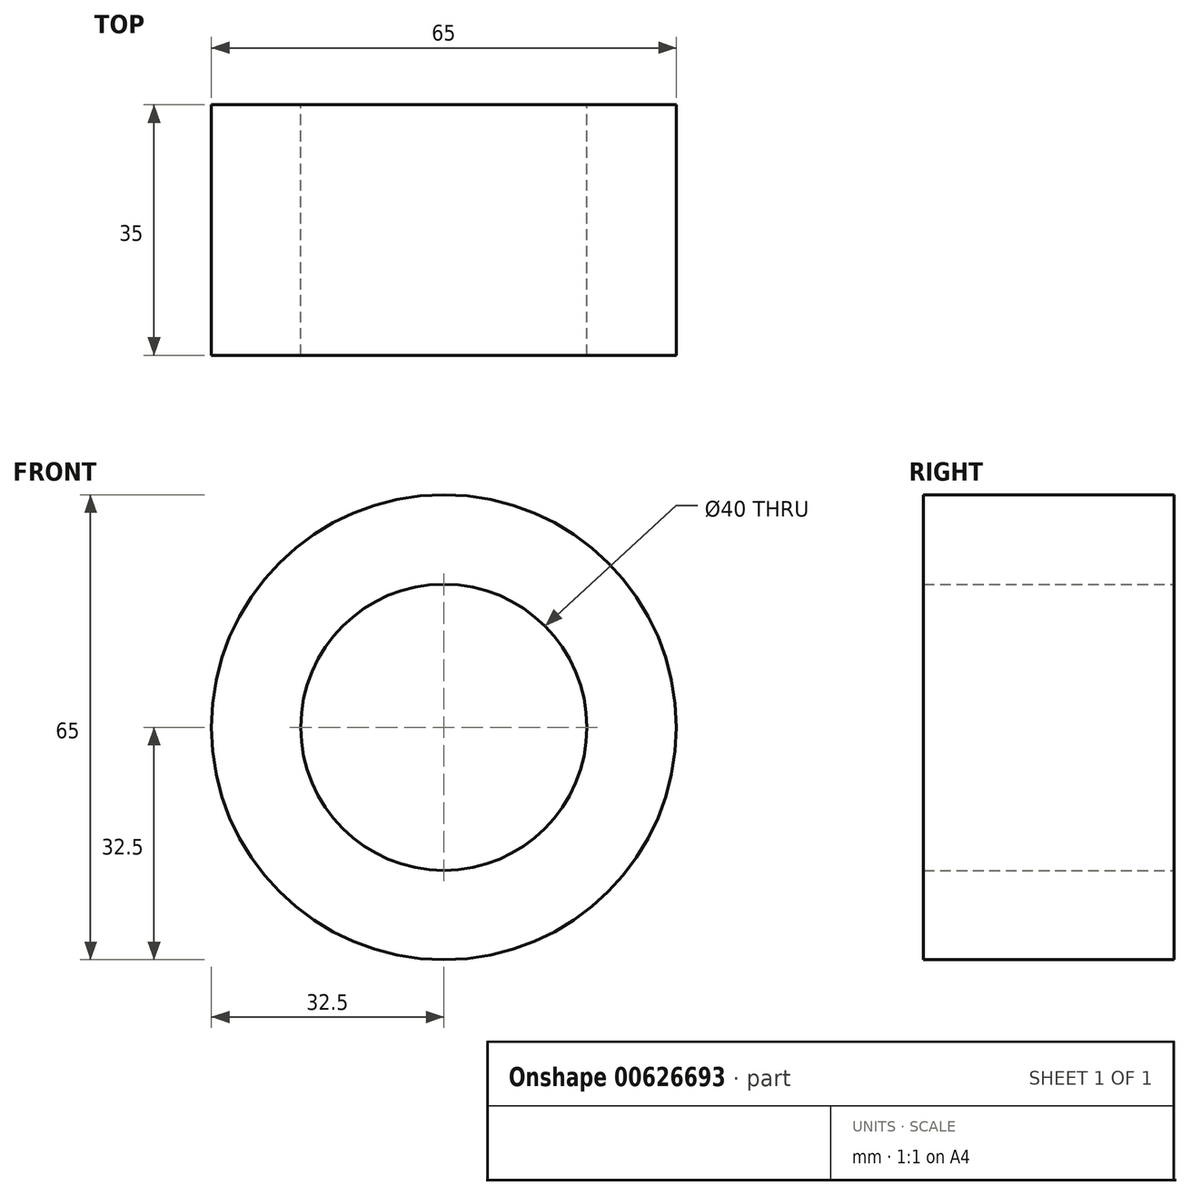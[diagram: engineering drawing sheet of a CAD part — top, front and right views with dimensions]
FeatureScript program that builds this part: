
annotation { "Feature Type Name" : "Feature", "Feature Type Description" : "" }
export const myFeature = defineFeature(function(context is Context, id is Id, definition is map)
    precondition{}
    {
        {
            var Q0;
            Q0=qCreatedBy(makeId("Front.planeOp"),FACE);
            var sketch = newSketch(context, id + "F0", { "sketchPlane" : qUnion([Q0])});
            skCircle(sketch, "E0", {"center": v(0, 0) * mm, "radius": 20 * mm});
            skCircle(sketch, "E1", {"center": v(0, 0) * mm, "radius": 32.5 * mm});
            skSolve(sketch);
        }
        {
            var Q0;
            Q0=makeQuery(id+"F0.imprint","IMPRINT",FACE,{"disambiguationData":[TD([[makeQuery(id+"F0.imprint","IMPRINT",EDGE,{"derivedFrom":sQuery(id+"F0.wireOp",EDGE,"E0")}),-1.0]])]});
            extrude(context, id + "F1", {"entities" : qUnion([Q0]), "endBound" : BoundingType.SYMMETRIC, "depth" : 35 * mm, "offsetDistance" : 25 * mm});
        }
        {
            var Q0;
            Q0=qCreatedBy(makeId("Top.planeOp"),FACE);
            var sketch = newSketch(context, id + "F2", { "sketchPlane" : qUnion([Q0])});
            skLineSegment(sketch, "E2", {"start": v(-22.5, -11.5) * mm, "end": v(22.5, -11.5) * mm});
            skPoint(sketch, "E3.end.orphan", {"position": v(22.5, 0) * mm});
            skLineSegment(sketch, "E4", {"start": v(-22.5, -11.5) * mm, "end": v(-22.5, 12.5) * mm});
            skLineSegment(sketch, "E5", {"start": v(22.5, -11.5) * mm, "end": v(22.5, 12.5) * mm});
            skPoint(sketch, "E6.end.orphan", {"position": v(-22.5, 11.5) * mm});
            skLineSegment(sketch, "E7", {"start": v(-22.5, 12.5) * mm, "end": v(22.5, 12.5) * mm});
            skSolve(sketch);
        }
        {
            var Q0;
            Q0=sQuery(id+"F2.wireOp",EDGE,"E4");
            var Q1;
            Q1=sQuery(id+"F2.wireOp",EDGE,"E7");
            var Q2;
            Q2=sQuery(id+"F2.wireOp",EDGE,"E5");
            var Q3;
            Q3=sQuery(id+"F2.wireOp",EDGE,"E2");
            extrude(context, id + "F3", {"bodyType" : ToolBodyType.SURFACE, "surfaceEntities" : qUnion([Q0, Q1, Q2, Q3]), "depth" : 144.8 * mm, "offsetDistance" : 25 * mm});
        }
    });
